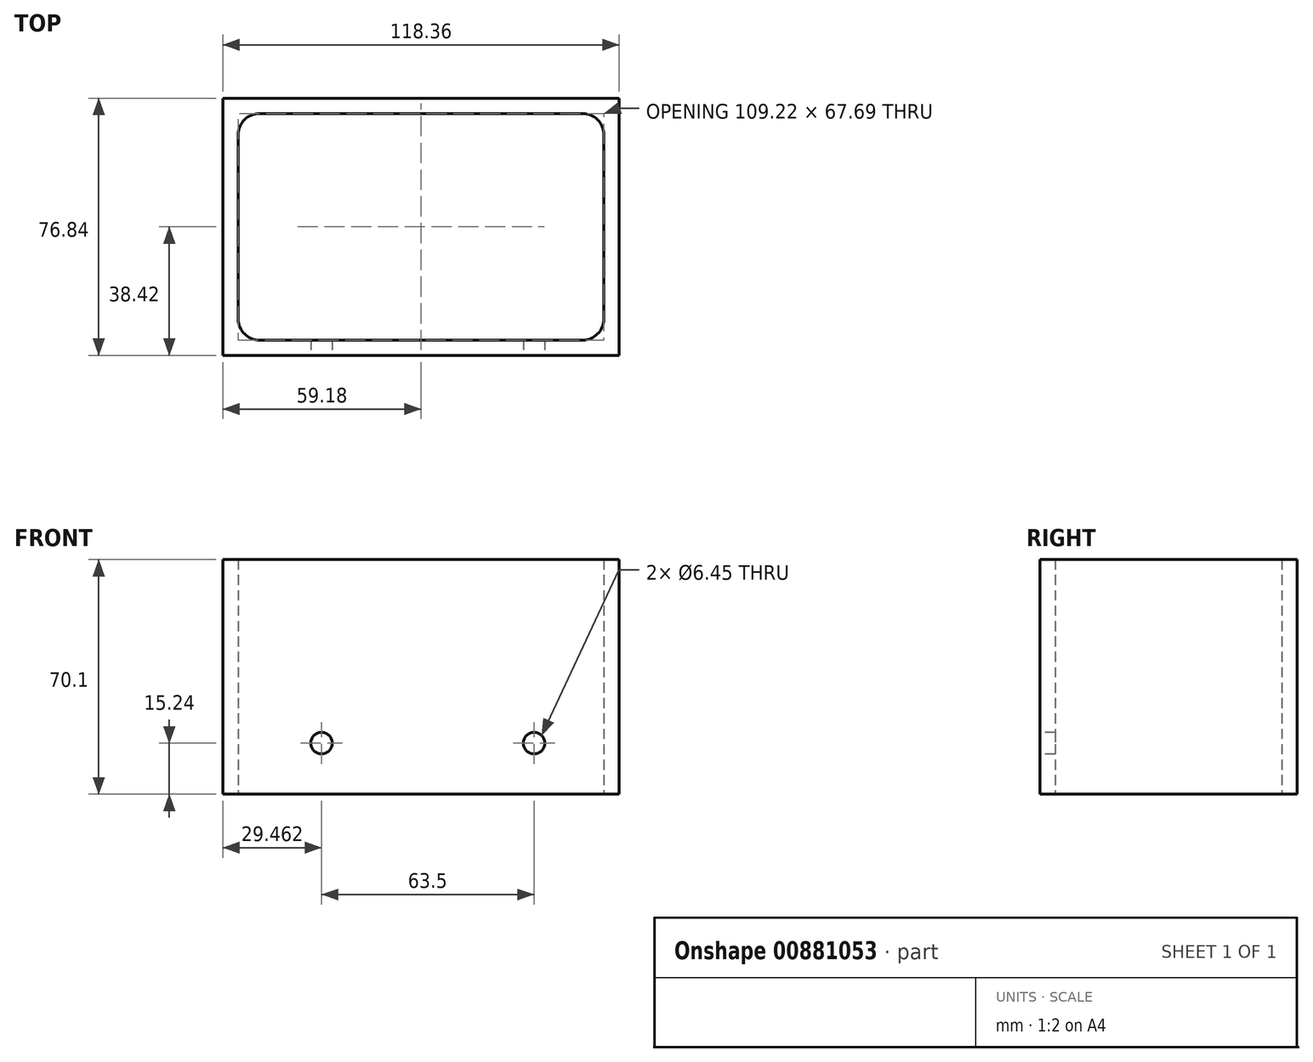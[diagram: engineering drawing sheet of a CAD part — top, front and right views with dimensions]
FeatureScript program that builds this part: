
annotation { "Feature Type Name" : "Feature", "Feature Type Description" : "" }
export const myFeature = defineFeature(function(context is Context, id is Id, definition is map)
    precondition{}
    {
        {
            var Q0;
            Q0=qCreatedBy(makeId("Top.planeOp"),FACE);
            var sketch = newSketch(context, id + "F0", { "sketchPlane" : qUnion([Q0])});
            skLineSegment(sketch, "E0.bottom", {"start": v(59.18, 38.42) * mm, "end": v(-59.18, 38.42) * mm});
            skLineSegment(sketch, "E0.top", {"start": v(59.18, -38.42) * mm, "end": v(-59.18, -38.42) * mm});
            skLineSegment(sketch, "E0.left", {"start": v(59.18, 38.42) * mm, "end": v(59.18, -38.42) * mm});
            skLineSegment(sketch, "E0.right", {"start": v(-59.18, 38.42) * mm, "end": v(-59.18, -38.42) * mm});
            skPoint(sketch, "E0.middle", {"position": v(0, 0) * mm});
            skLineSegment(sketch, "E1.bottom", {"start": v(-48.26, 33.85) * mm, "end": v(48.26, 33.85) * mm});
            skLineSegment(sketch, "E1.top", {"start": v(-48.26, -33.85) * mm, "end": v(48.26, -33.85) * mm});
            skLineSegment(sketch, "E1.left", {"start": v(-54.61, 27.5) * mm, "end": v(-54.61, -27.5) * mm});
            skLineSegment(sketch, "E1.right", {"start": v(54.61, 27.5) * mm, "end": v(54.61, -27.5) * mm});
            skPoint(sketch, "E2.visualSharp", {"position": v(-54.61, 33.85) * mm});
            skArc(sketch, "E2.filletArc", {"start": v(-48.26, 33.85) * mm, "mid": v(-52.75, 31.99) * mm, "end": v(-54.61, 27.5) * mm});
            skPoint(sketch, "E3.visualSharp", {"position": v(-54.61, -33.85) * mm});
            skArc(sketch, "E3.filletArc", {"start": v(-54.61, -27.5) * mm, "mid": v(-52.75, -31.99) * mm, "end": v(-48.26, -33.85) * mm});
            skPoint(sketch, "E4.visualSharp", {"position": v(54.61, -33.85) * mm});
            skArc(sketch, "E4.filletArc", {"start": v(48.26, -33.85) * mm, "mid": v(52.75, -31.99) * mm, "end": v(54.61, -27.5) * mm});
            skPoint(sketch, "E5.visualSharp", {"position": v(54.61, 33.85) * mm});
            skArc(sketch, "E5.filletArc", {"start": v(54.61, 27.5) * mm, "mid": v(52.75, 31.99) * mm, "end": v(48.26, 33.85) * mm});
            skSolve(sketch);
        }
        {
            var Q0;
            Q0 = qSketchRegion(id + "F0", true);
            extrude(context, id + "F1", {"entities" : qUnion([Q0]), "depth" : 70.1 * mm, "offsetDistance" : 25.4 * mm});
        }
        {
            var Q0;
            Q0=makeQuery(id+"F1.opExtrude","SWEPT_FACE",FACE,{"disambiguationData":[OSD([sQuery(id+"F0.wireOp",EDGE,"E0.top")])]});
            var sketch = newSketch(context, id + "F2", { "sketchPlane" : qUnion([Q0])});
            skCircle(sketch, "E6", {"center": v(33.78, 15.24) * mm, "radius": 3.23 * mm});
            skCircle(sketch, "E7", {"center": v(-29.72, 15.24) * mm, "radius": 3.23 * mm});
            skSolve(sketch);
        }
        {
            var Q0;
            Q0 = qSketchRegion(id + "F2", true);
            extrude(context, id + "F3", {"entities" : qUnion([Q0]), "operationType" : NewBodyOperationType.REMOVE, "oppositeDirection" : true, "depth" : 25.4 * mm, "offsetDistance" : 25.4 * mm});
        }
    });
